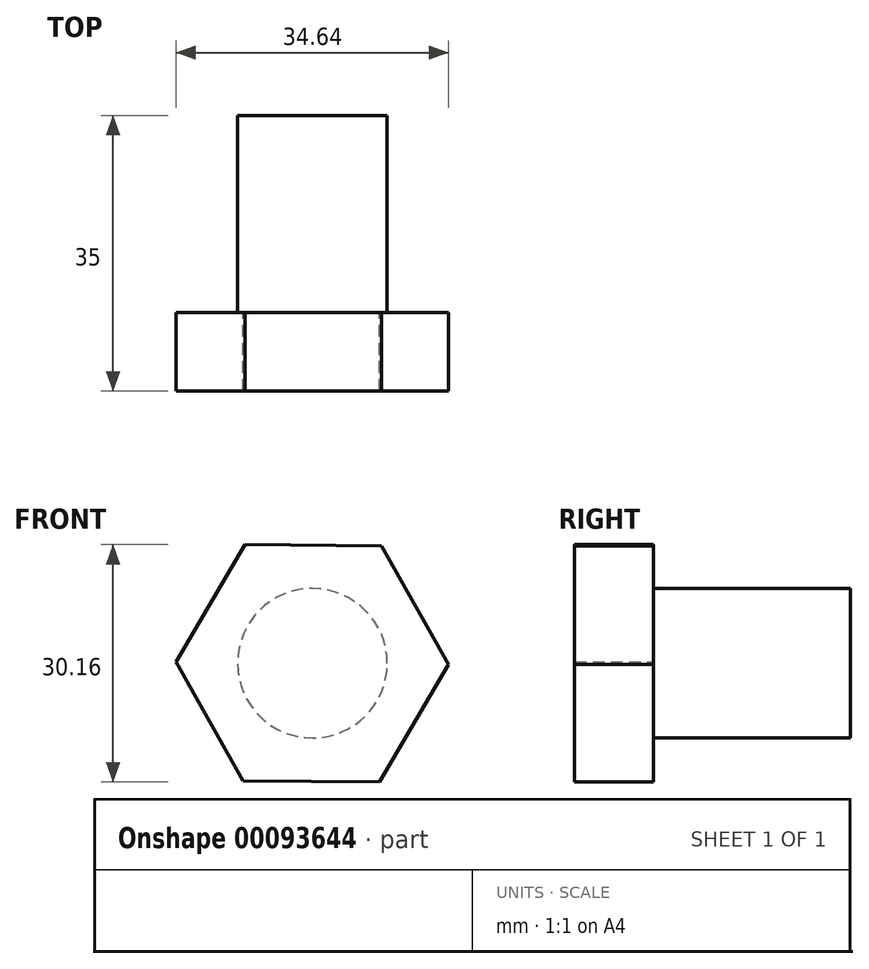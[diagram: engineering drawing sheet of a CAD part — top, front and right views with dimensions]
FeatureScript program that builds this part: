
annotation { "Feature Type Name" : "Feature", "Feature Type Description" : "" }
export const myFeature = defineFeature(function(context is Context, id is Id, definition is map)
    precondition{}
    {
        {
            var Q0;
            Q0=qCreatedBy(makeId("Front.planeOp"),FACE);
            var sketch = newSketch(context, id + "F0", { "sketchPlane" : qUnion([Q0])});
            skCircle(sketch, "E0", {"center": v(0, 0) * mm, "radius": 9.5 * mm});
            skSolve(sketch);
        }
        {
            var Q0;
            Q0 = qSketchRegion(id + "F0", true);
            extrude(context, id + "F1", {"entities" : qUnion([Q0]), "depth" : 25 * mm});
        }
        {
            var Q0;
            Q0=makeQuery(id+"F1.opExtrude","CAP_FACE",FACE,{"disambiguationData":[OSD([sQuery(id+"F0.wireOp",EDGE,"E0")])],"isStart":false});
            var sketch = newSketch(context, id + "F2", { "sketchPlane" : qUnion([Q0])});
            skCircle(sketch, "E1.cCircle", {"center": v(0, 0) * mm, "radius": 15 * mm, "construction": true});
            skLineSegment(sketch, "E1.0", {"start": v(17.32, -0.16) * mm, "end": v(8.52, -15.08) * mm});
            skLineSegment(sketch, "E1.1", {"start": v(8.52, -15.08) * mm, "end": v(-8.8, -14.92) * mm});
            skLineSegment(sketch, "E1.2", {"start": v(-8.8, -14.92) * mm, "end": v(-17.32, 0.16) * mm});
            skLineSegment(sketch, "E1.3", {"start": v(-17.32, 0.16) * mm, "end": v(-8.52, 15.08) * mm});
            skLineSegment(sketch, "E1.4", {"start": v(-8.52, 15.08) * mm, "end": v(8.8, 14.92) * mm});
            skLineSegment(sketch, "E1.5", {"start": v(8.8, 14.92) * mm, "end": v(17.32, -0.16) * mm});
            skPoint(sketch, "E1.0.midPoint", {"position": v(12.92, -7.62) * mm});
            skSolve(sketch);
        }
        {
            var Q0;
            Q0 = qSketchRegion(id + "F2", true);
            extrude(context, id + "F3", {"entities" : qUnion([Q0]), "operationType" : NewBodyOperationType.ADD, "depth" : 10 * mm});
        }
    });
